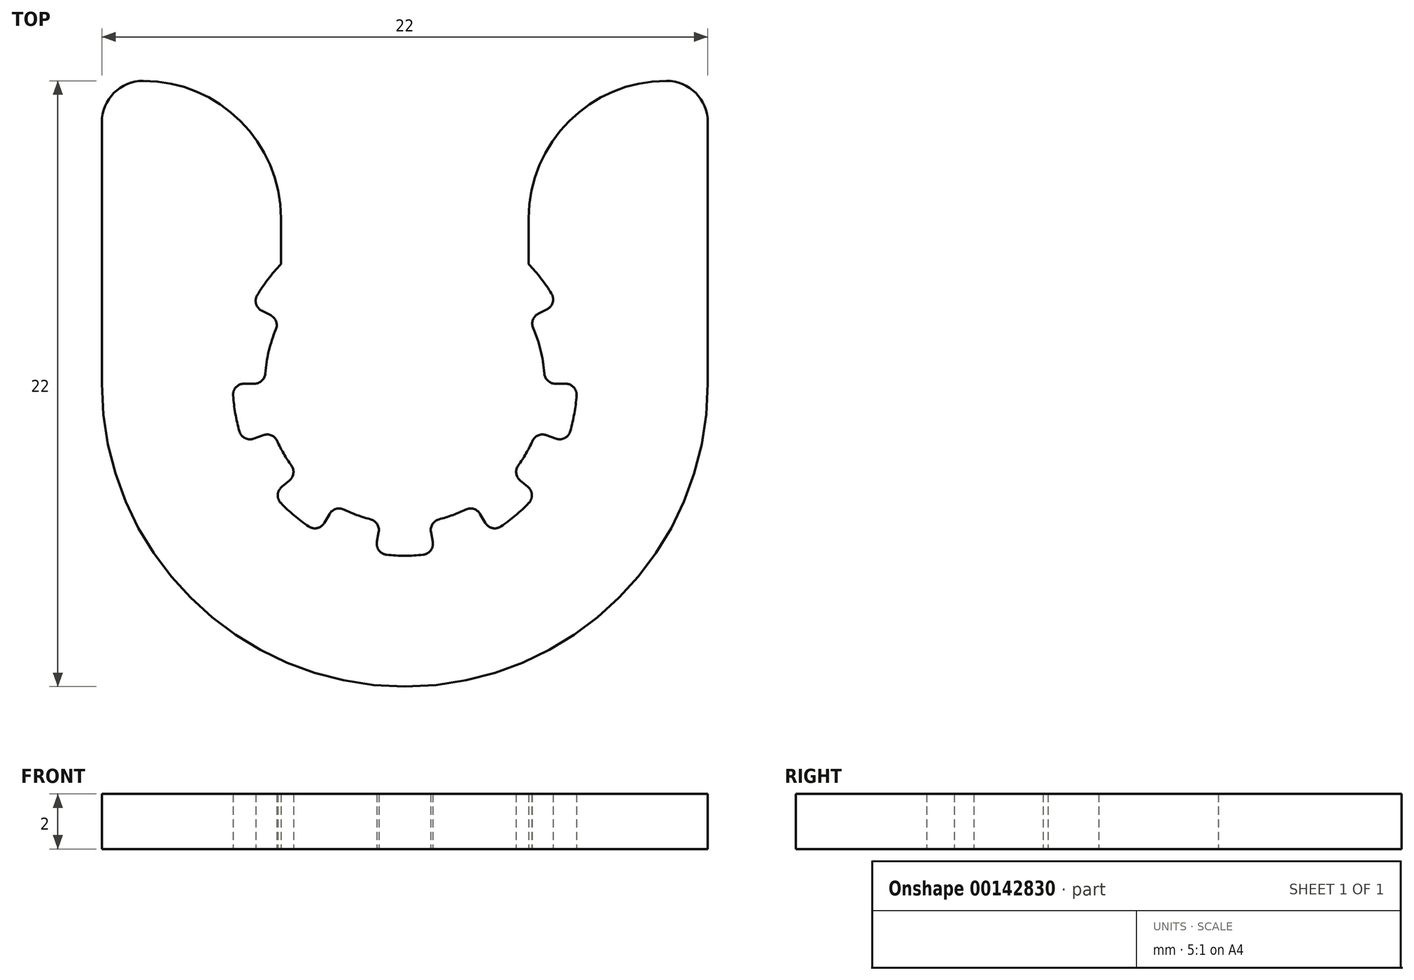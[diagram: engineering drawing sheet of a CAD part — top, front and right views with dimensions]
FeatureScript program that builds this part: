
annotation { "Feature Type Name" : "Feature", "Feature Type Description" : "" }
export const myFeature = defineFeature(function(context is Context, id is Id, definition is map)
    precondition{}
    {
        {
            var Q0;
            Q0=qCreatedBy(makeId("Top.planeOp"),FACE);
            var sketch = newSketch(context, id + "F0", { "sketchPlane" : qUnion([Q0])});
            skArc(sketch, "E0", {"start": v(-4.68, 1.97) * mm, "mid": v(-4.94, 1.19) * mm, "end": v(-5.07, 0.37) * mm});
            skArc(sketch, "E1", {"start": v(-11, 0) * mm, "mid": v(0, -11) * mm, "end": v(11, 0) * mm});
            skLineSegment(sketch, "E2.left", {"start": v(-11, 0) * mm, "end": v(-11, 9.5) * mm});
            skLineSegment(sketch, "E2.right", {"start": v(11, 0) * mm, "end": v(11, 9.5) * mm});
            skLineSegment(sketch, "E3", {"start": v(-9.5, 11) * mm, "end": v(-9.5, 11) * mm});
            skLineSegment(sketch, "E4", {"start": v(-4.5, 4.34) * mm, "end": v(-4.5, 6) * mm});
            skLineSegment(sketch, "E5", {"start": v(4.5, 4.34) * mm, "end": v(4.5, 6) * mm});
            skLineSegment(sketch, "E6.trimOffspring", {"start": v(9.5, 11) * mm, "end": v(9.5, 11) * mm});
            skPoint(sketch, "E7.orphan", {"position": v(-4.5, 19.15) * mm});
            skPoint(sketch, "E8.orphan", {"position": v(4.5, 18.53) * mm});
            skPoint(sketch, "E9.third.point", {"position": v(-104.28, 11) * mm});
            skPoint(sketch, "E10.third.point", {"position": v(64.61, 54.62) * mm});
            skPoint(sketch, "E11.orphan", {"position": v(4.5, 0) * mm});
            skPoint(sketch, "E12.orphan", {"position": v(-4.5, 0) * mm});
            skArc(sketch, "E13", {"start": v(-6.24, -0.43) * mm, "mid": v(-6.16, -1.09) * mm, "end": v(-6, -1.73) * mm});
            skLineSegment(sketch, "E14", {"start": v(-5.47, 0) * mm, "end": v(-5.84, 0) * mm});
            skLineSegment(sketch, "E15", {"start": v(5.47, 0) * mm, "end": v(5.84, 0) * mm});
            skLineSegment(sketch, "E16", {"start": v(-5.14, -1.87) * mm, "end": v(-5.48, -2) * mm});
            skArc(sketch, "E17.trimOffspring", {"start": v(-4.63, -2.08) * mm, "mid": v(-4.4, -2.54) * mm, "end": v(-4.12, -2.97) * mm});
            skLineSegment(sketch, "E18", {"start": v(-4.19, -3.51) * mm, "end": v(-4.47, -3.75) * mm});
            skLineSegment(sketch, "E19", {"start": v(-2.73, -4.73) * mm, "end": v(-2.92, -5.05) * mm});
            skLineSegment(sketch, "E20", {"start": v(-0.95, -5.38) * mm, "end": v(-1.01, -5.75) * mm});
            skArc(sketch, "E21.trimOffspring", {"start": v(-2.21, -4.57) * mm, "mid": v(-1.74, -4.77) * mm, "end": v(-1.24, -4.93) * mm});
            skLineSegment(sketch, "E22", {"start": v(0.95, -5.38) * mm, "end": v(1.01, -5.75) * mm});
            skArc(sketch, "E23.trimOffspring", {"start": v(1.24, -4.93) * mm, "mid": v(1.74, -4.77) * mm, "end": v(2.21, -4.57) * mm});
            skArc(sketch, "E24.trimOffspring", {"start": v(-0.66, -6.21) * mm, "mid": v(0, -6.25) * mm, "end": v(0.66, -6.21) * mm});
            skArc(sketch, "E25.trimOffspring", {"start": v(-4.5, -4.34) * mm, "mid": v(-4.02, -4.79) * mm, "end": v(-3.49, -5.19) * mm});
            skLineSegment(sketch, "E26", {"start": v(2.73, -4.73) * mm, "end": v(2.92, -5.05) * mm});
            skArc(sketch, "E27.trimOffspring", {"start": v(3.49, -5.19) * mm, "mid": v(4.02, -4.79) * mm, "end": v(4.5, -4.34) * mm});
            skLineSegment(sketch, "E28", {"start": v(4.19, -3.51) * mm, "end": v(4.47, -3.75) * mm});
            skLineSegment(sketch, "E29", {"start": v(5.14, -1.87) * mm, "end": v(5.48, -2) * mm});
            skArc(sketch, "E30.trimOffspring", {"start": v(4.12, -2.97) * mm, "mid": v(4.4, -2.54) * mm, "end": v(4.63, -2.08) * mm});
            skArc(sketch, "E31.trimOffspring", {"start": v(5.07, 0.37) * mm, "mid": v(4.93, 1.21) * mm, "end": v(4.66, 2.02) * mm});
            skArc(sketch, "E32.trimOffspring", {"start": v(6, -1.73) * mm, "mid": v(6.16, -1.09) * mm, "end": v(6.24, -0.43) * mm});
            skLineSegment(sketch, "E33", {"start": v(4.84, 2.54) * mm, "end": v(5.17, 2.7) * mm});
            skLineSegment(sketch, "E34", {"start": v(-4.87, 2.48) * mm, "end": v(-5.2, 2.65) * mm});
            skArc(sketch, "E35.trimOffspring", {"start": v(-4.5, 4.34) * mm, "mid": v(-4.96, 3.8) * mm, "end": v(-5.36, 3.21) * mm});
            skPoint(sketch, "E36.visualSharp", {"position": v(4.5, 11) * mm});
            skArc(sketch, "E36.filletArc", {"start": v(9.5, 11) * mm, "mid": v(5.96, 9.54) * mm, "end": v(4.5, 6) * mm});
            skPoint(sketch, "E37.visualSharp", {"position": v(-4.5, 11) * mm});
            skArc(sketch, "E37.filletArc", {"start": v(-4.5, 6) * mm, "mid": v(-5.96, 9.54) * mm, "end": v(-9.5, 11) * mm});
            skPoint(sketch, "E38.visualSharp", {"position": v(11, 11) * mm});
            skArc(sketch, "E38.filletArc", {"start": v(11, 9.5) * mm, "mid": v(10.56, 10.56) * mm, "end": v(9.5, 11) * mm});
            skPoint(sketch, "E39.visualSharp", {"position": v(-11, 11) * mm});
            skArc(sketch, "E39.filletArc", {"start": v(-9.5, 11) * mm, "mid": v(-10.56, 10.56) * mm, "end": v(-11, 9.5) * mm});
            skArc(sketch, "E40.trimOffspring", {"start": v(5.33, 3.27) * mm, "mid": v(4.94, 3.83) * mm, "end": v(4.5, 4.34) * mm});
            skPoint(sketch, "E41.visualSharp", {"position": v(-5.57, 2.84) * mm});
            skArc(sketch, "E41.filletArc", {"start": v(-5.36, 3.21) * mm, "mid": v(-5.4, 2.9) * mm, "end": v(-5.2, 2.65) * mm});
            skPoint(sketch, "E42.visualSharp", {"position": v(5.54, 2.9) * mm});
            skArc(sketch, "E42.filletArc", {"start": v(5.17, 2.7) * mm, "mid": v(5.37, 2.96) * mm, "end": v(5.33, 3.27) * mm});
            skPoint(sketch, "E43.visualSharp", {"position": v(6.25, 0) * mm});
            skArc(sketch, "E43.filletArc", {"start": v(6.24, -0.43) * mm, "mid": v(6.13, -0.13) * mm, "end": v(5.84, 0) * mm});
            skPoint(sketch, "E44.visualSharp", {"position": v(5.87, -2.14) * mm});
            skArc(sketch, "E44.filletArc", {"start": v(5.48, -2) * mm, "mid": v(5.8, -1.98) * mm, "end": v(6, -1.73) * mm});
            skPoint(sketch, "E45.visualSharp", {"position": v(4.79, -4.02) * mm});
            skArc(sketch, "E45.filletArc", {"start": v(4.5, -4.34) * mm, "mid": v(4.61, -4.04) * mm, "end": v(4.47, -3.75) * mm});
            skPoint(sketch, "E46.visualSharp", {"position": v(3.12, -5.41) * mm});
            skArc(sketch, "E46.filletArc", {"start": v(2.92, -5.05) * mm, "mid": v(3.17, -5.24) * mm, "end": v(3.49, -5.19) * mm});
            skPoint(sketch, "E47.visualSharp", {"position": v(1.09, -6.16) * mm});
            skArc(sketch, "E47.filletArc", {"start": v(0.66, -6.21) * mm, "mid": v(0.94, -6.06) * mm, "end": v(1.01, -5.75) * mm});
            skPoint(sketch, "E48.visualSharp", {"position": v(-1.09, -6.16) * mm});
            skArc(sketch, "E48.filletArc", {"start": v(-1.01, -5.75) * mm, "mid": v(-0.94, -6.06) * mm, "end": v(-0.66, -6.21) * mm});
            skPoint(sketch, "E49.visualSharp", {"position": v(-3.12, -5.41) * mm});
            skArc(sketch, "E49.filletArc", {"start": v(-3.49, -5.19) * mm, "mid": v(-3.17, -5.24) * mm, "end": v(-2.92, -5.05) * mm});
            skPoint(sketch, "E50.visualSharp", {"position": v(-4.79, -4.02) * mm});
            skArc(sketch, "E50.filletArc", {"start": v(-4.47, -3.75) * mm, "mid": v(-4.61, -4.04) * mm, "end": v(-4.5, -4.34) * mm});
            skPoint(sketch, "E51.visualSharp", {"position": v(-5.87, -2.14) * mm});
            skArc(sketch, "E51.filletArc", {"start": v(-6, -1.73) * mm, "mid": v(-5.8, -1.98) * mm, "end": v(-5.48, -2) * mm});
            skPoint(sketch, "E52.visualSharp", {"position": v(-6.25, 0) * mm});
            skArc(sketch, "E52.filletArc", {"start": v(-5.84, 0) * mm, "mid": v(-6.13, -0.13) * mm, "end": v(-6.24, -0.43) * mm});
            skPoint(sketch, "E53.visualSharp", {"position": v(-4.77, -1.74) * mm});
            skArc(sketch, "E53.filletArc", {"start": v(-4.63, -2.08) * mm, "mid": v(-4.84, -1.88) * mm, "end": v(-5.14, -1.87) * mm});
            skPoint(sketch, "E54.visualSharp", {"position": v(-3.9, -3.27) * mm});
            skArc(sketch, "E54.filletArc", {"start": v(-4.19, -3.51) * mm, "mid": v(-4.05, -3.26) * mm, "end": v(-4.12, -2.97) * mm});
            skPoint(sketch, "E55.visualSharp", {"position": v(-2.54, -4.4) * mm});
            skArc(sketch, "E55.filletArc", {"start": v(-2.21, -4.57) * mm, "mid": v(-2.5, -4.55) * mm, "end": v(-2.73, -4.73) * mm});
            skPoint(sketch, "E56.visualSharp", {"position": v(-0.88, -5) * mm});
            skArc(sketch, "E56.filletArc", {"start": v(-0.95, -5.38) * mm, "mid": v(-1, -5.1) * mm, "end": v(-1.24, -4.93) * mm});
            skPoint(sketch, "E57.visualSharp", {"position": v(0.88, -5) * mm});
            skArc(sketch, "E57.filletArc", {"start": v(1.24, -4.93) * mm, "mid": v(1, -5.1) * mm, "end": v(0.95, -5.38) * mm});
            skPoint(sketch, "E58.visualSharp", {"position": v(2.54, -4.4) * mm});
            skArc(sketch, "E58.filletArc", {"start": v(2.73, -4.73) * mm, "mid": v(2.5, -4.55) * mm, "end": v(2.21, -4.57) * mm});
            skPoint(sketch, "E59.visualSharp", {"position": v(3.9, -3.27) * mm});
            skArc(sketch, "E59.filletArc", {"start": v(4.12, -2.97) * mm, "mid": v(4.05, -3.26) * mm, "end": v(4.19, -3.51) * mm});
            skPoint(sketch, "E60.visualSharp", {"position": v(5.08, 0) * mm});
            skArc(sketch, "E60.filletArc", {"start": v(5.07, 0.37) * mm, "mid": v(5.2, 0.1) * mm, "end": v(5.47, 0) * mm});
            skPoint(sketch, "E61.visualSharp", {"position": v(4.77, -1.74) * mm});
            skArc(sketch, "E61.filletArc", {"start": v(5.14, -1.87) * mm, "mid": v(4.84, -1.88) * mm, "end": v(4.63, -2.08) * mm});
            skPoint(sketch, "E62.visualSharp", {"position": v(4.5, 2.36) * mm});
            skArc(sketch, "E62.filletArc", {"start": v(4.84, 2.54) * mm, "mid": v(4.65, 2.31) * mm, "end": v(4.66, 2.02) * mm});
            skPoint(sketch, "E63.visualSharp", {"position": v(-5.08, 0) * mm});
            skArc(sketch, "E63.filletArc", {"start": v(-5.47, 0) * mm, "mid": v(-5.2, 0.1) * mm, "end": v(-5.07, 0.37) * mm});
            skArc(sketch, "E64.filletArc", {"start": v(-4.68, 1.97) * mm, "mid": v(-4.67, 2.26) * mm, "end": v(-4.87, 2.48) * mm});
            skSolve(sketch);
        }
        {
            var Q0;
            Q0 = qSketchRegion(id + "F0", true);
            extrude(context, id + "F1", {"entities" : qUnion([Q0]), "depth" : 2 * mm, "offsetDistance" : 25 * mm});
        }
    });
